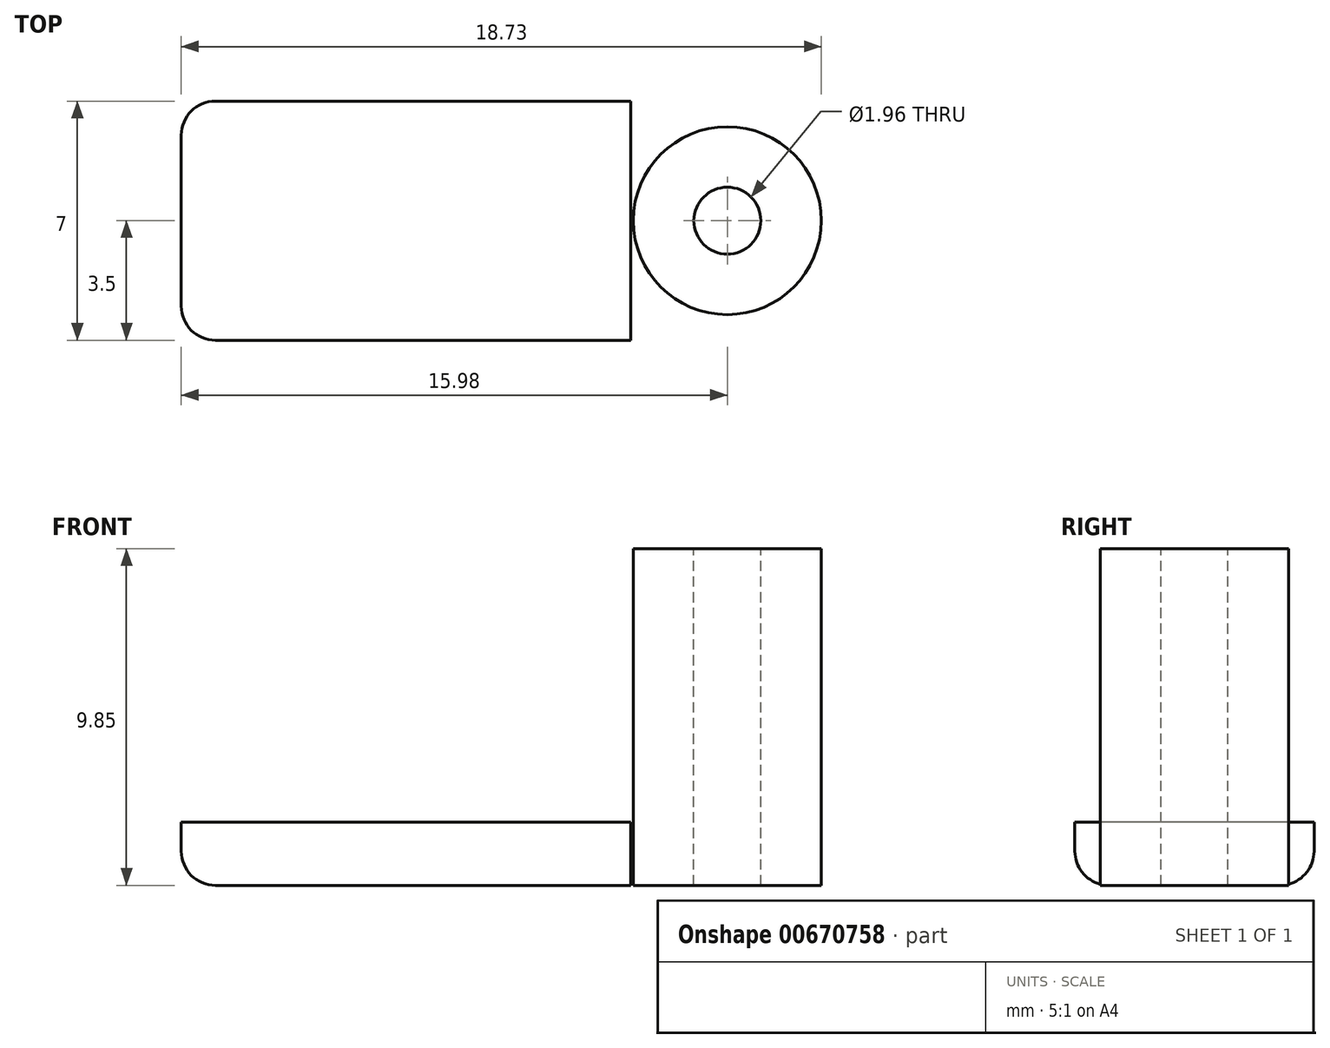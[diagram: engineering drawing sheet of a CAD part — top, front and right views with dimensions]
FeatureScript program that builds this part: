
annotation { "Feature Type Name" : "Feature", "Feature Type Description" : "" }
export const myFeature = defineFeature(function(context is Context, id is Id, definition is map)
    precondition{}
    {
        {
            var Q0;
            Q0=qCreatedBy(makeId("Top.planeOp"),FACE);
            var sketch = newSketch(context, id + "F0", { "sketchPlane" : qUnion([Q0])});
            skLineSegment(sketch, "E0.bottom", {"start": v(7.5, 3.5) * mm, "end": v(-7.5, 3.5) * mm});
            skLineSegment(sketch, "E0.top", {"start": v(7.5, -3.5) * mm, "end": v(-7.5, -3.5) * mm});
            skLineSegment(sketch, "E0.left", {"start": v(7.5, 3.5) * mm, "end": v(7.5, -3.5) * mm});
            skLineSegment(sketch, "E0.right", {"start": v(-7.5, 3.5) * mm, "end": v(-7.5, -3.5) * mm});
            skPoint(sketch, "E0.middle", {"position": v(0, 0) * mm});
            skCircle(sketch, "E1", {"center": v(8.48, 0) * mm, "radius": 0.98 * mm});
            skPoint(sketch, "E2", {"position": v(7.5, 0) * mm});
            skCircle(sketch, "E3", {"center": v(8.48, 0) * mm, "radius": 2.75 * mm});
            skLineSegment(sketch, "E4.bottom", {"start": v(-7.5, 3.5) * mm, "end": v(-5.65, 3.5) * mm});
            skLineSegment(sketch, "E4.top", {"start": v(-7.5, -3.5) * mm, "end": v(-5.65, -3.5) * mm});
            skLineSegment(sketch, "E4.right", {"start": v(-5.65, 3.5) * mm, "end": v(-5.65, -3.5) * mm});
            skLineSegment(sketch, "E5.bottom", {"start": v(7.5, 3.5) * mm, "end": v(5.65, 3.5) * mm});
            skLineSegment(sketch, "E5.top", {"start": v(7.5, -3.5) * mm, "end": v(5.65, -3.5) * mm});
            skLineSegment(sketch, "E5.right", {"start": v(5.65, 3.5) * mm, "end": v(5.65, -3.5) * mm});
            skSolve(sketch);
        }
        {
            var Q0;
            Q0=makeQuery(id+"F0.imprint","IMPRINT",FACE,{"disambiguationData":[TD([[makeQuery(id+"F0.imprint","IMPRINT",EDGE,{"derivedFrom":sQuery(id+"F0.wireOp",EDGE,"E4.bottom")}),-1.0]])]});
            var Q1;
            Q1=makeQuery(id+"F0.imprint","IMPRINT",FACE,{"disambiguationData":[TD([[makeQuery(id+"F0.imprint","IMPRINT",EDGE,{"derivedFrom":sQuery(id+"F0.wireOp",EDGE,"E0.bottom")}),1.0]])]});
            var Q2;
            {var subQ0=sQuery(id+"F0.wireOp",EDGE,"E0.left");var subQ1=sQuery(id+"F0.wireOp",EDGE,"E3");var subQ2=makeQuery(id+"F0.imprint","INTERSECT",VERTEX,{"disambiguationData":[OD(0.0)],"derivedFrom":[subQ1,subQ0]});Q2=makeQuery(id+"F0.imprint","IMPRINT",FACE,{"disambiguationData":[TD([[makeQuery(id+"F0.imprint","IMPRINT",EDGE,{"disambiguationData":[TD([[subQ2,-1.0]])],"derivedFrom":subQ1}),1.0]])]});}
            var Q3;
            {var subQ1=sQuery(id+"F0.wireOp",EDGE,"E5.bottom");Q3=makeQuery(id+"F0.imprint","IMPRINT",FACE,{"disambiguationData":[TD([[makeQuery(id+"F0.imprint","IMPRINT",EDGE,{"derivedFrom":subQ1}),1.0]])]});}
            var Q4;
            {var subQ0=sQuery(id+"F0.wireOp",EDGE,"E1");Q4=makeQuery(id+"F0.imprint","IMPRINT",FACE,{"disambiguationData":[TD([[makeQuery(id+"F0.imprint","IMPRINT",EDGE,{"derivedFrom":subQ0}),-1.0]])]});}
            extrude(context, id + "F1", {"entities" : qUnion([Q0, Q1, Q2, Q3, Q4]), "oppositeDirection" : true, "depth" : 1.85 * mm, "offsetDistance" : 25 * mm});
        }
        {
            var Q0;
            Q0=makeQuery(id+"F0.imprint","IMPRINT",FACE,{"disambiguationData":[TD([[makeQuery(id+"F0.imprint","IMPRINT",EDGE,{"derivedFrom":sQuery(id+"F0.wireOp",EDGE,"E4.bottom")}),-1.0]])]});
            var Q1;
            {var subQ1=sQuery(id+"F0.wireOp",EDGE,"E5.bottom");Q1=makeQuery(id+"F0.imprint","IMPRINT",FACE,{"disambiguationData":[TD([[makeQuery(id+"F0.imprint","IMPRINT",EDGE,{"derivedFrom":subQ1}),1.0]])]});}
            var Q2;
            {var subQ0=sQuery(id+"F0.wireOp",EDGE,"E0.left");var subQ1=sQuery(id+"F0.wireOp",EDGE,"E3");var subQ2=makeQuery(id+"F0.imprint","INTERSECT",VERTEX,{"disambiguationData":[OD(0.0)],"derivedFrom":[subQ1,subQ0]});Q2=makeQuery(id+"F0.imprint","IMPRINT",FACE,{"disambiguationData":[TD([[makeQuery(id+"F0.imprint","IMPRINT",EDGE,{"disambiguationData":[TD([[subQ2,-1.0]])],"derivedFrom":subQ1}),1.0]])]});}
            var Q3;
            {var subQ0=sQuery(id+"F0.wireOp",EDGE,"E1");Q3=makeQuery(id+"F0.imprint","IMPRINT",FACE,{"disambiguationData":[TD([[makeQuery(id+"F0.imprint","IMPRINT",EDGE,{"derivedFrom":subQ0}),-1.0]])]});}
            extrude(context, id + "F2", {"entities" : qUnion([Q0, Q1, Q2, Q3]), "operationType" : NewBodyOperationType.ADD, "depth" : 8 * mm, "offsetDistance" : 25 * mm});
        }
        {
            var Q0;
            Q0=makeQuery(id+"F2.opExtrude","CAP_EDGE",EDGE,{"disambiguationData":[OSD([sQuery(id+"F0.wireOp",EDGE,"E4.right")])],"isStart":true});
            var Q1;
            Q1=makeQuery(id+"F2.opExtrude","CAP_EDGE",EDGE,{"disambiguationData":[OSD([sQuery(id+"F0.wireOp",EDGE,"E5.right")])],"isStart":true});
            var Q2;
            Q2=makeQuery(id+"F1.opExtrude","CAP_EDGE",EDGE,{"disambiguationData":[OSD([sQuery(id+"F0.wireOp",EDGE,"E0.right")])],"isStart":false});
            var Q3;
            {var subQ0=sQuery(id+"F0.wireOp",EDGE,"E0.left");var subQ1=sQuery(id+"F0.wireOp",EDGE,"E3");var subQ2=makeQuery(id+"F0.imprint","INTERSECT",VERTEX,{"disambiguationData":[OD(0.0)],"derivedFrom":[subQ1,subQ0]});Q3=makeQuery(id+"F2.boolean.opBoolean","MERGE",EDGE,{"derivedFrom":[makeQuery(id+"F1.opExtrude","SWEPT_EDGE",EDGE,{"disambiguationData":[OSD([subQ1,subQ0]),TDD([subQ2])]}),makeQuery(id+"F2.opExtrude","SWEPT_EDGE",EDGE,{"disambiguationData":[OSD([subQ1,subQ0]),TDD([subQ2])]})]});}
            var Q4;
            {var subQ0=sQuery(id+"F0.wireOp",EDGE,"E0.left");var subQ1=sQuery(id+"F0.wireOp",EDGE,"E3");var subQ2=makeQuery(id+"F0.imprint","INTERSECT",VERTEX,{"disambiguationData":[OD(1.0)],"derivedFrom":[subQ1,subQ0]});Q4=makeQuery(id+"F2.boolean.opBoolean","MERGE",EDGE,{"derivedFrom":[makeQuery(id+"F1.opExtrude","SWEPT_EDGE",EDGE,{"disambiguationData":[OSD([subQ1,subQ0]),TDD([subQ2])]}),makeQuery(id+"F2.opExtrude","SWEPT_EDGE",EDGE,{"disambiguationData":[OSD([subQ1,subQ0]),TDD([subQ2])]})]});}
            fillet(context, id + "F3", {"entities" : qUnion([Q0, Q1, Q2, Q3, Q4]), "radius" : 1 * mm, "tangentPropagation" : true, "allowEdgeOverflow" : false});
        }
        {
            var Q0;
            {var subQ0=sQuery(id+"F0.wireOp",EDGE,"E0.right");var subQ1=sQuery(id+"F0.wireOp",EDGE,"E4.bottom");Q0=makeQuery(id+"F2.boolean.opBoolean","MERGE",EDGE,{"derivedFrom":[makeQuery(id+"F1.opExtrude","SWEPT_EDGE",EDGE,{"disambiguationData":[OSD([subQ1,subQ0])]}),makeQuery(id+"F2.opExtrude","SWEPT_EDGE",EDGE,{"disambiguationData":[OSD([subQ1,subQ0])]})]});}
            var Q1;
            Q1=makeQuery(id+"F1.opExtrude","CAP_EDGE",EDGE,{"disambiguationData":[OSD([sQuery(id+"F0.wireOp",EDGE,"E0.bottom"),sQuery(id+"F0.wireOp",EDGE,"E4.bottom"),sQuery(id+"F0.wireOp",EDGE,"E5.bottom")])],"isStart":false});
            var Q2;
            {var subQ0=sQuery(id+"F0.wireOp",EDGE,"E5.bottom");var subQ1=sQuery(id+"F0.wireOp",EDGE,"E4.bottom");Q2=makeQuery(id+"F3.opFillet","BLEND_EDGE",EDGE,{"blendedFrom":[makeQuery(id+"F1.opExtrude","CAP_EDGE",EDGE,{"disambiguationData":[OSD([sQuery(id+"F0.wireOp",EDGE,"E0.right")])],"isStart":false}),makeQuery(id+"F2.boolean.opBoolean","MERGE",FACE,{"derivedFrom":[makeQuery(id+"F1.opExtrude","SWEPT_FACE",FACE,{"disambiguationData":[OSD([sQuery(id+"F0.wireOp",EDGE,"E0.bottom"),subQ1,subQ0])]}),makeQuery(id+"F2.opExtrude","SWEPT_FACE",FACE,{"disambiguationData":[OSD([subQ1])]}),makeQuery(id+"F2.opExtrude","SWEPT_FACE",FACE,{"disambiguationData":[OSD([subQ0])]})]})],"blendedInto":[makeQuery(id+"F2.boolean.opBoolean","MERGE",FACE,{"derivedFrom":[makeQuery(id+"F1.opExtrude","SWEPT_FACE",FACE,{"disambiguationData":[OSD([sQuery(id+"F0.wireOp",EDGE,"E0.bottom"),subQ1,subQ0])]}),makeQuery(id+"F2.opExtrude","SWEPT_FACE",FACE,{"disambiguationData":[OSD([subQ1])]}),makeQuery(id+"F2.opExtrude","SWEPT_FACE",FACE,{"disambiguationData":[OSD([subQ0])]})]})]});}
            var Q3;
            {var subQ0=sQuery(id+"F0.wireOp",EDGE,"E5.bottom");var subQ1=sQuery(id+"F0.wireOp",EDGE,"E4.bottom");var subQ2=sQuery(id+"F0.wireOp",EDGE,"E0.left");var subQ3=sQuery(id+"F0.wireOp",EDGE,"E3");var subQ4=makeQuery(id+"F0.imprint","INTERSECT",VERTEX,{"disambiguationData":[OD(0.0)],"derivedFrom":[subQ3,subQ2]});Q3=makeQuery(id+"F3.opFillet","BLEND_EDGE",EDGE,{"blendedFrom":[makeQuery(id+"F2.boolean.opBoolean","MERGE",EDGE,{"derivedFrom":[makeQuery(id+"F1.opExtrude","SWEPT_EDGE",EDGE,{"disambiguationData":[OSD([subQ3,subQ2]),TDD([subQ4])]}),makeQuery(id+"F2.opExtrude","SWEPT_EDGE",EDGE,{"disambiguationData":[OSD([subQ3,subQ2]),TDD([subQ4])]})]}),makeQuery(id+"F2.boolean.opBoolean","MERGE",FACE,{"derivedFrom":[makeQuery(id+"F1.opExtrude","SWEPT_FACE",FACE,{"disambiguationData":[OSD([sQuery(id+"F0.wireOp",EDGE,"E0.bottom"),subQ1,subQ0])]}),makeQuery(id+"F2.opExtrude","SWEPT_FACE",FACE,{"disambiguationData":[OSD([subQ1])]}),makeQuery(id+"F2.opExtrude","SWEPT_FACE",FACE,{"disambiguationData":[OSD([subQ0])]})]})],"blendedInto":[makeQuery(id+"F2.boolean.opBoolean","MERGE",FACE,{"derivedFrom":[makeQuery(id+"F1.opExtrude","SWEPT_FACE",FACE,{"disambiguationData":[OSD([sQuery(id+"F0.wireOp",EDGE,"E0.bottom"),subQ1,subQ0])]}),makeQuery(id+"F2.opExtrude","SWEPT_FACE",FACE,{"disambiguationData":[OSD([subQ1])]}),makeQuery(id+"F2.opExtrude","SWEPT_FACE",FACE,{"disambiguationData":[OSD([subQ0])]})]})]});}
            var Q4;
            {var subQ0=sQuery(id+"F0.wireOp",EDGE,"E0.right");var subQ1=sQuery(id+"F0.wireOp",EDGE,"E4.top");Q4=makeQuery(id+"F2.boolean.opBoolean","MERGE",EDGE,{"derivedFrom":[makeQuery(id+"F1.opExtrude","SWEPT_EDGE",EDGE,{"disambiguationData":[OSD([subQ1,subQ0])]}),makeQuery(id+"F2.opExtrude","SWEPT_EDGE",EDGE,{"disambiguationData":[OSD([subQ1,subQ0])]})]});}
            var Q5;
            {var subQ0=sQuery(id+"F0.wireOp",EDGE,"E5.top");var subQ1=sQuery(id+"F0.wireOp",EDGE,"E4.top");var subQ2=sQuery(id+"F0.wireOp",EDGE,"E0.left");var subQ3=sQuery(id+"F0.wireOp",EDGE,"E3");var subQ4=makeQuery(id+"F0.imprint","INTERSECT",VERTEX,{"disambiguationData":[OD(1.0)],"derivedFrom":[subQ3,subQ2]});Q5=makeQuery(id+"F3.opFillet","BLEND_EDGE",EDGE,{"blendedFrom":[makeQuery(id+"F2.boolean.opBoolean","MERGE",EDGE,{"derivedFrom":[makeQuery(id+"F1.opExtrude","SWEPT_EDGE",EDGE,{"disambiguationData":[OSD([subQ3,subQ2]),TDD([subQ4])]}),makeQuery(id+"F2.opExtrude","SWEPT_EDGE",EDGE,{"disambiguationData":[OSD([subQ3,subQ2]),TDD([subQ4])]})]}),makeQuery(id+"F2.boolean.opBoolean","MERGE",FACE,{"derivedFrom":[makeQuery(id+"F1.opExtrude","SWEPT_FACE",FACE,{"disambiguationData":[OSD([sQuery(id+"F0.wireOp",EDGE,"E0.top"),subQ1,subQ0])]}),makeQuery(id+"F2.opExtrude","SWEPT_FACE",FACE,{"disambiguationData":[OSD([subQ1])]}),makeQuery(id+"F2.opExtrude","SWEPT_FACE",FACE,{"disambiguationData":[OSD([subQ0])]})]})],"blendedInto":[makeQuery(id+"F2.boolean.opBoolean","MERGE",FACE,{"derivedFrom":[makeQuery(id+"F1.opExtrude","SWEPT_FACE",FACE,{"disambiguationData":[OSD([sQuery(id+"F0.wireOp",EDGE,"E0.top"),subQ1,subQ0])]}),makeQuery(id+"F2.opExtrude","SWEPT_FACE",FACE,{"disambiguationData":[OSD([subQ1])]}),makeQuery(id+"F2.opExtrude","SWEPT_FACE",FACE,{"disambiguationData":[OSD([subQ0])]})]})]});}
            var Q6;
            Q6=makeQuery(id+"F1.opExtrude","CAP_EDGE",EDGE,{"disambiguationData":[OSD([sQuery(id+"F0.wireOp",EDGE,"E0.top"),sQuery(id+"F0.wireOp",EDGE,"E4.top"),sQuery(id+"F0.wireOp",EDGE,"E5.top")])],"isStart":false});
            fillet(context, id + "F4", {"entities" : qUnion([Q0, Q1, Q2, Q3, Q4, Q5, Q6]), "radius" : 1 * mm, "tangentPropagation" : true, "allowEdgeOverflow" : false});
        }
    });
